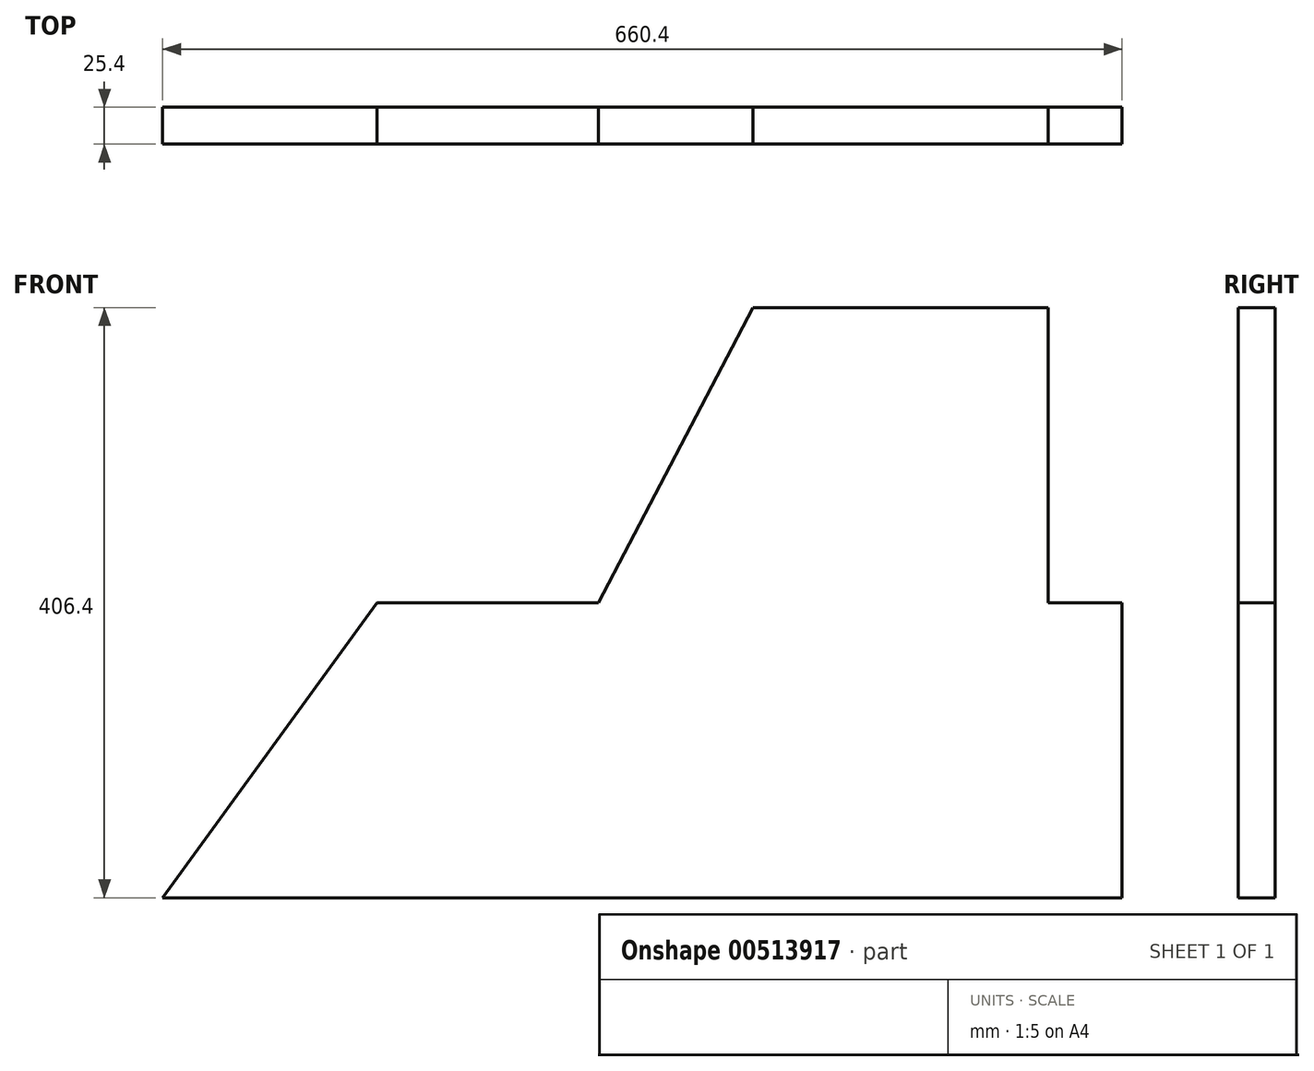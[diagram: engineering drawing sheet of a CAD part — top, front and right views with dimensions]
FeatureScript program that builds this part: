
annotation { "Feature Type Name" : "Feature", "Feature Type Description" : "" }
export const myFeature = defineFeature(function(context is Context, id is Id, definition is map)
    precondition{}
    {
        {
            var Q0;
            Q0=qCreatedBy(makeId("Front.planeOp"),FACE);
            var sketch = newSketch(context, id + "F0", { "sketchPlane" : qUnion([Q0])});
            skLineSegment(sketch, "E0", {"start": v(-64.26, -42.1) * mm, "end": v(596.14, -42.1) * mm});
            skLineSegment(sketch, "E1", {"start": v(596.14, -42.1) * mm, "end": v(596.14, 161.1) * mm});
            skLineSegment(sketch, "E2", {"start": v(596.14, 161.1) * mm, "end": v(545.34, 161.1) * mm});
            skLineSegment(sketch, "E3", {"start": v(545.34, 161.1) * mm, "end": v(545.34, 364.3) * mm});
            skLineSegment(sketch, "E4", {"start": v(545.34, 364.3) * mm, "end": v(342.14, 364.3) * mm});
            skLineSegment(sketch, "E5", {"start": v(342.14, 364.3) * mm, "end": v(235.57, 161.1) * mm});
            skLineSegment(sketch, "E6", {"start": v(235.57, 161.1) * mm, "end": v(83.17, 161.1) * mm});
            skLineSegment(sketch, "E7", {"start": v(83.17, 161.1) * mm, "end": v(-64.26, -42.1) * mm});
            skSolve(sketch);
        }
        {
            var Q0;
            Q0=makeQuery(id+"F0.imprint","IMPRINT",FACE,{"disambiguationData":[TD([[makeQuery(id+"F0.imprint","IMPRINT",EDGE,{"derivedFrom":sQuery(id+"F0.wireOp",EDGE,"E0")}),1.0]])]});
            extrude(context, id + "F1", {"entities" : qUnion([Q0]), "depth" : 25.4 * mm, "offsetDistance" : 25.4 * mm});
        }
    });
